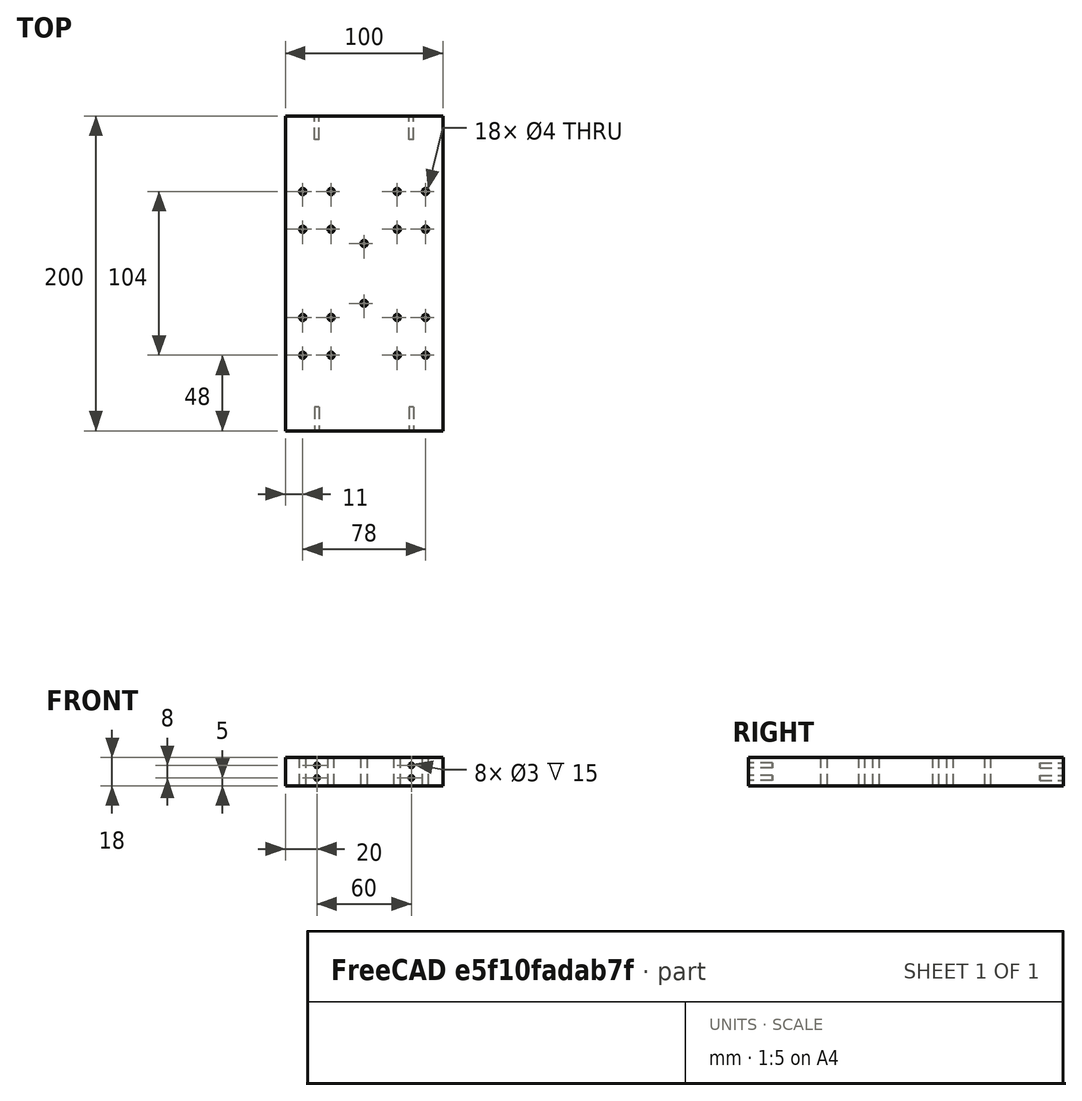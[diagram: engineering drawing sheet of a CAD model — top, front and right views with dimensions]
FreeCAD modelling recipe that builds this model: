
FCSTD DOCUMENT  (FreeCAD 0.17R13541 (Git))
Label: Z-Central
License: All rights reserved
LicenseURL: http://en.wikipedia.org/wiki/All_rights_reserved
objects: Part::Cylinder×22, Part::Cut×10, Part::MultiFuse×7, Part::Box×4, Part::Mirroring×2
note: 45 computed .brp shape members not serialized (recipe doc carries the construction recipe); baked Part::Feature solids carry a one-line shape summary decoded from their .brp

FEATURE [Part::Box] Box  label="BaseIzquierda"
  AttacherType = Attacher::AttachEngine3D
  Height = 18
  Length = 50
  Width = 100
FEATURE [Part::Cylinder] Cylinder  label="Cilindro"
  Angle = 360
  AttacherType = Attacher::AttachEngine3D
  Height = 25
  Placement = pos=(11,48,0) rot=(0,0,1;0rad)
  Radius = 2
FEATURE [Part::Cylinder] Cylinder001  label="Cilindro001"
  Angle = 360
  AttacherType = Attacher::AttachEngine3D
  Height = 25
  Placement = pos=(11,72,0) rot=(0,0,1;0rad)
  Radius = 2
FEATURE [Part::Cylinder] Cylinder002  label="Cilindro002"
  Angle = 360
  AttacherType = Attacher::AttachEngine3D
  Height = 25
  Placement = pos=(29,48,0) rot=(0,0,1;0rad)
  Radius = 2
FEATURE [Part::Cylinder] Cylinder003  label="Cilindro003"
  Angle = 360
  AttacherType = Attacher::AttachEngine3D
  Height = 25
  Placement = pos=(29,72,0) rot=(0,0,1;0rad)
  Radius = 2
FEATURE [Part::MultiFuse] Fusion  label="Huecos"
  Refine = true
  Shapes = -> [Cylinder,Cylinder001,Cylinder002,Cylinder003]
FEATURE [Part::Box] Box001  label="BaseDerecha"
  AttacherType = Attacher::AttachEngine3D
  Height = 18
  Length = 50
  Placement = pos=(-50,0,0) rot=(0,0,1;0rad)
  Width = 100
FEATURE [Part::Cylinder] Cylinder004  label="Cilindro004"
  Angle = 360
  AttacherType = Attacher::AttachEngine3D
  Height = 25
  Placement = pos=(11,48,0) rot=(0,0,1;0rad)
  Radius = 2
FEATURE [Part::Cylinder] Cylinder005  label="Cilindro005"
  Angle = 360
  AttacherType = Attacher::AttachEngine3D
  Height = 25
  Placement = pos=(11,72,0) rot=(0,0,1;0rad)
  Radius = 2
FEATURE [Part::Cylinder] Cylinder006  label="Cilindro006"
  Angle = 360
  AttacherType = Attacher::AttachEngine3D
  Height = 25
  Placement = pos=(29,48,0) rot=(0,0,1;0rad)
  Radius = 2
FEATURE [Part::Cylinder] Cylinder007  label="Cilindro007"
  Angle = 360
  AttacherType = Attacher::AttachEngine3D
  Height = 25
  Placement = pos=(29,72,0) rot=(0,0,1;0rad)
  Radius = 2
FEATURE [Part::MultiFuse] Fusion001  label="Huecos001"
  Placement = pos=(-40,0,0) rot=(0,0,1;0rad)
  Refine = true
  Shapes = -> [Cylinder004,Cylinder005,Cylinder006,Cylinder007]
FEATURE [Part::Box] Box002  label="BaseIzquierda001"
  AttacherType = Attacher::AttachEngine3D
  Height = 18
  Length = 50
  Placement = pos=(0,100,0) rot=(0,0,1;0rad)
  Width = 100
FEATURE [Part::Box] Box003  label="BaseIzquierda002"
  AttacherType = Attacher::AttachEngine3D
  Height = 18
  Length = 50
  Placement = pos=(-50,100,0) rot=(0,0,1;0rad)
  Width = 100
FEATURE [Part::Cylinder] Cylinder008  label="Cilindro008"
  Angle = 360
  AttacherType = Attacher::AttachEngine3D
  Height = 25
  Placement = pos=(11,48,0) rot=(0,0,1;0rad)
  Radius = 2
FEATURE [Part::Cylinder] Cylinder009  label="Cilindro009"
  Angle = 360
  AttacherType = Attacher::AttachEngine3D
  Height = 25
  Placement = pos=(11,72,0) rot=(0,0,1;0rad)
  Radius = 2
FEATURE [Part::Cylinder] Cylinder010  label="Cilindro010"
  Angle = 360
  AttacherType = Attacher::AttachEngine3D
  Height = 25
  Placement = pos=(29,48,0) rot=(0,0,1;0rad)
  Radius = 2
FEATURE [Part::Cylinder] Cylinder011  label="Cilindro011"
  Angle = 360
  AttacherType = Attacher::AttachEngine3D
  Height = 25
  Placement = pos=(29,72,0) rot=(0,0,1;0rad)
  Radius = 2
FEATURE [Part::MultiFuse] Fusion002  label="Huecos002"
  Placement = pos=(-40,80,0) rot=(0,0,1;0rad)
  Refine = true
  Shapes = -> [Cylinder008,Cylinder009,Cylinder010,Cylinder011]
FEATURE [Part::Cylinder] Cylinder012  label="Cilindro012"
  Angle = 360
  AttacherType = Attacher::AttachEngine3D
  Height = 25
  Placement = pos=(11,48,0) rot=(0,0,1;0rad)
  Radius = 2
FEATURE [Part::Cylinder] Cylinder013  label="Cilindro013"
  Angle = 360
  AttacherType = Attacher::AttachEngine3D
  Height = 25
  Placement = pos=(11,72,0) rot=(0,0,1;0rad)
  Radius = 2
FEATURE [Part::Cylinder] Cylinder014  label="Cilindro014"
  Angle = 360
  AttacherType = Attacher::AttachEngine3D
  Height = 25
  Placement = pos=(29,48,0) rot=(0,0,1;0rad)
  Radius = 2
FEATURE [Part::Cylinder] Cylinder015  label="Cilindro015"
  Angle = 360
  AttacherType = Attacher::AttachEngine3D
  Height = 25
  Placement = pos=(29,72,0) rot=(0,0,1;0rad)
  Radius = 2
FEATURE [Part::MultiFuse] Fusion003  label="Huecos003"
  Placement = pos=(0,80,0) rot=(0,0,1;0rad)
  Refine = true
  Shapes = -> [Cylinder012,Cylinder013,Cylinder014,Cylinder015]
FEATURE [Part::Cut] Cut
  Base = -> Box002
  Refine = true
  Tool = -> Fusion003
FEATURE [Part::Cut] Cut001
  Base = -> Box003
  Placement = pos=(100,0,0) rot=(0,0,1;0rad)
  Refine = true
  Tool = -> Fusion002
FEATURE [Part::Cut] Cut002
  Base = -> Box001
  Placement = pos=(100,0,0) rot=(0,0,1;0rad)
  Refine = true
  Tool = -> Fusion001
FEATURE [Part::Cut] Cut003
  Base = -> Box
  Refine = true
  Tool = -> Fusion
FEATURE [Part::Cylinder] Cylinder016  label="HuecoCentral1"
  Angle = 360
  AttacherType = Attacher::AttachEngine3D
  Height = 25
  Placement = pos=(50,81,0) rot=(0,0,1;0rad)
  Radius = 2
FEATURE [Part::Cylinder] Cylinder017  label="HuecoCentral2"
  Angle = 360
  AttacherType = Attacher::AttachEngine3D
  Height = 25
  Placement = pos=(50,119,0) rot=(0,0,1;0rad)
  Radius = 2
FEATURE [Part::MultiFuse] Fusion004
  Refine = true
  Shapes = -> [Cut002,Cut003,Cut,Cut001]
FEATURE [Part::Cut] Cut004
  Base = -> Fusion004
  Refine = true
  Tool = -> Cylinder016
FEATURE [Part::Cut] Cut005
  Base = -> Cut004
  Refine = true
  Tool = -> Cylinder017
FEATURE [Part::Cylinder] Cylinder018  label="Cilindro016"
  Angle = 360
  AttacherType = Attacher::AttachEngine3D
  Height = 15
  Placement = pos=(20,15,9) rot=(1,0,0;1.5708rad)
  Radius = 1.5
FEATURE [Part::Cylinder] Cylinder019  label="Cilindro017"
  Angle = 360
  AttacherType = Attacher::AttachEngine3D
  Height = 15
  Placement = pos=(80,15,9) rot=(1,0,0;1.5708rad)
  Radius = 1.5
FEATURE [Part::MultiFuse] Fusion005
  Placement = pos=(0,0,-4) rot=(0,0,1;0rad)
  Refine = true
  Shapes = -> [Cylinder019,Cylinder018]
FEATURE [Part::Mirroring] mirror  label="Mirror of Fusion005"
  Base = (80,100,18)
  Normal = (0,-0.73037,0)
  Source = -> Fusion005
FEATURE [Part::Cut] Cut006
  Base = -> Cut005
  Refine = true
  Tool = -> mirror
FEATURE [Part::Cut] Cut007
  Base = -> Cut006
  Refine = true
  Tool = -> Fusion005
FEATURE [Part::Cylinder] Cylinder020  label="Cilindro018"
  Angle = 360
  AttacherType = Attacher::AttachEngine3D
  Height = 15
  Placement = pos=(80,15,9) rot=(1,0,0;1.5708rad)
  Radius = 1.5
FEATURE [Part::Cylinder] Cylinder021  label="Cilindro019"
  Angle = 360
  AttacherType = Attacher::AttachEngine3D
  Height = 15
  Placement = pos=(20,15,9) rot=(1,0,0;1.5708rad)
  Radius = 1.5
FEATURE [Part::MultiFuse] Fusion006
  Placement = pos=(0,0,4) rot=(0,0,1;0rad)
  Refine = true
  Shapes = -> [Cylinder020,Cylinder021]
FEATURE [Part::Mirroring] mirror001  label="Mirror of Fusion006"
  Base = (0,100,18)
  Normal = (0,0.45,0)
  Source = -> Fusion006
FEATURE [Part::Cut] Cut008
  Base = -> Cut007
  Refine = true
  Tool = -> Fusion006
FEATURE [Part::Cut] Cut009
  Base = -> Cut008
  Refine = true
  Tool = -> mirror001
